# Revit family: Nominal Cut Lumber-Section
name_source: partatom
category: Detail Items
revit_build: Autodesk Revit Architecture 2012 (Build: 20110210_1515)
units: mm (PartAtom-declared; Revit-internal decimal feet)

## types (29) — shared parameters

## per-type parameters (varying)
| type | Depth | Keynote | Width |
| 1x3 | 0' - 2 1/2" | 06 11 00.B3 | 0' - 0 3/4" |
| 1x4 | 0' - 3 1/2" | 06 11 00.B5 | 0' - 0 3/4" |
| 1x5 | 0' - 4 1/2" | 06 11 00.B7 | 0' - 0 3/4" |
| 1x6 | 0' - 5 1/2" | 06 11 00.B8 | 0' - 0 3/4" |
| 1x8 | 0' - 7 1/4" | 06 11 00.B10 | 0' - 0 3/4" |
| 1x10 | 0' - 9 1/4" | 06 11 00.B12 | 0' - 0 3/4" |
| 1x12 | 0' - 11 1/4" | 06 11 00.B13 | 0' - 0 3/4" |
| 2x3 | 0' - 2 1/2" | 06 11 00.C1 | 0' - 1 1/2" |
| 2x4 | 0' - 3 1/2" | 06 11 00.D1 | 0' - 1 1/2" |
| 2x5 | 0' - 4 1/2" | 06 11 00.E1 | 0' - 1 1/2" |
| 2x6 | 0' - 5 1/2" | 06 11 00.F1 | 0' - 1 1/2" |
| 2x8 | 0' - 7 1/4" | 06 11 00.G1 | 0' - 1 1/2" |
| 2x10 | 0' - 9 1/4" | 06 11 00.H1 | 0' - 1 1/2" |
| 2x12 | 0' - 11 1/4" | 06 11 00.I1 | 0' - 1 1/2" |
| 2x14 | 1' - 1 1/4" | 06 11 00.J1 | 0' - 1 1/2" |
| 3x4 | 0' - 3 1/2" | 06 11 00.K1 | 0' - 2 1/2" |
| 3x6 | 0' - 5 1/2" | 06 11 00.K2 | 0' - 2 1/2" |
| 3x8 | 0' - 7 1/4" | 06 11 00.K3 | 0' - 2 1/2" |
| 3x10 | 0' - 9 1/4" | 06 11 00.K4 | 0' - 2 1/2" |
| 3x12 | 0' - 11 1/4" | 06 11 00.K5 | 0' - 2 1/2" |
| 3x14 | 1' - 1 1/4" | 06 11 00.K6 | 0' - 2 1/2" |
| 3x16 | 1' - 3 1/4" | 06 11 00.K7 | 0' - 2 1/2" |
| 4x4 | 0' - 3 1/2" | 06 11 00.L1 | 0' - 3 1/2" |
| 4x6 | 0' - 5 1/2" | 06 11 00.L5 | 0' - 3 1/2" |
| 4x8 | 0' - 7 1/4" | 06 11 00.L6 | 0' - 3 1/2" |
| 4x10 | 0' - 9 1/4" | 06 11 00.L7 | 0' - 3 1/2" |
| 4x12 | 0' - 11 1/4" | 06 11 00.L8 | 0' - 3 1/2" |
| 4x14 | 1' - 1 1/2" | 06 11 00.L9 | 0' - 3 1/2" |
| 6x6 | 0' - 5 1/2" | 06 11 00.M1 | 0' - 5 1/2" |
